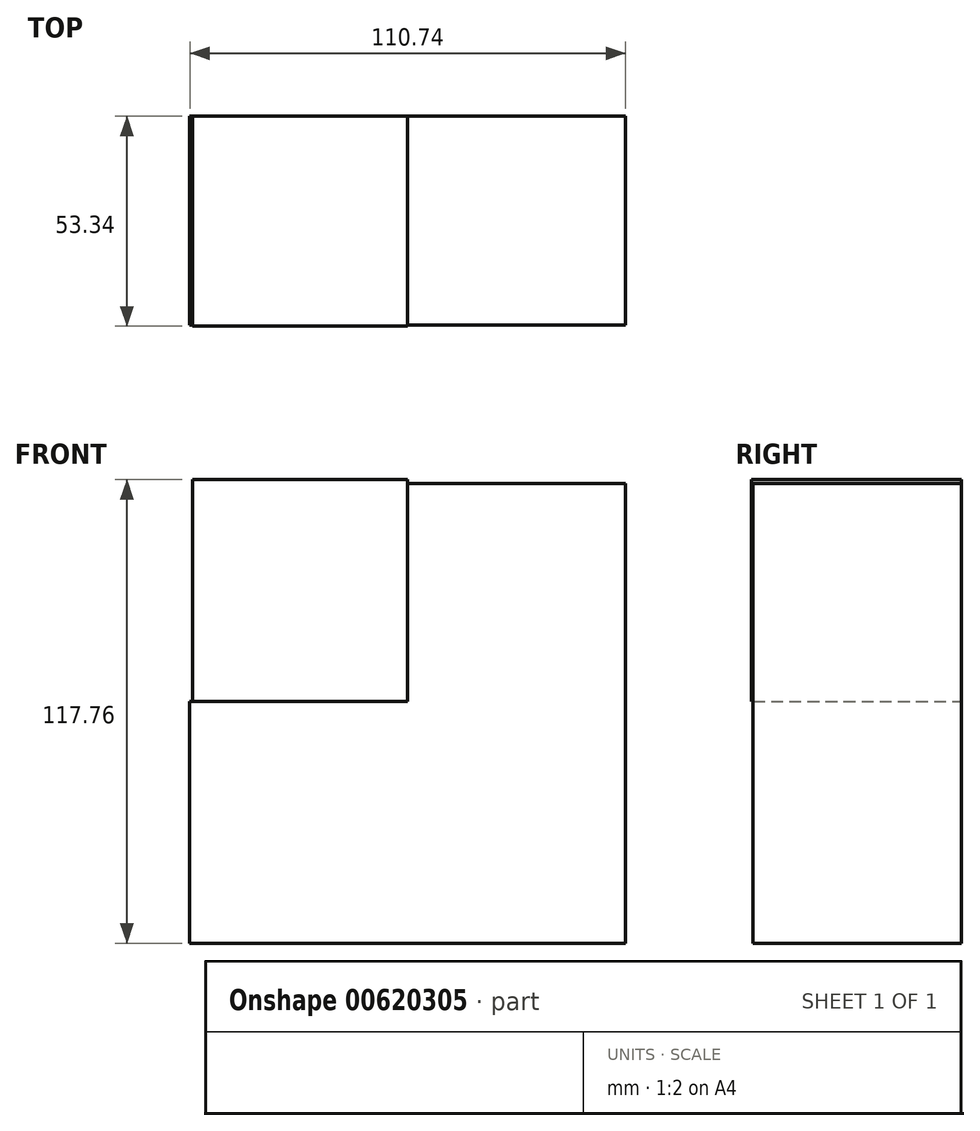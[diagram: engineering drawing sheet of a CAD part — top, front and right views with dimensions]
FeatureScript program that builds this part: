
annotation { "Feature Type Name" : "Feature", "Feature Type Description" : "" }
export const myFeature = defineFeature(function(context is Context, id is Id, definition is map)
    precondition{}
    {
        {
            var Q0;
            Q0=qCreatedBy(makeId("Right.planeOp"),FACE);
            var sketch = newSketch(context, id + "F0", { "sketchPlane" : qUnion([Q0])});
            skLineSegment(sketch, "E0.bottom", {"start": v(0, 0) * mm, "end": v(52.98, 0) * mm});
            skLineSegment(sketch, "E0.top", {"start": v(0, -61.46) * mm, "end": v(52.98, -61.46) * mm});
            skLineSegment(sketch, "E0.left", {"start": v(0, 0) * mm, "end": v(0, -61.46) * mm});
            skLineSegment(sketch, "E0.right", {"start": v(52.98, 0) * mm, "end": v(52.98, -61.46) * mm});
            skSolve(sketch);
        }
        {
            var Q0;
            Q0 = qSketchRegion(id + "F0", true);
            extrude(context, id + "F1", {"entities" : qUnion([Q0]), "oppositeDirection" : true, "depth" : 55.37 * mm, "offsetDistance" : 25.4 * mm});
        }
        {
            var Q0;
            Q0=makeQuery(id+"F1.opExtrude","SWEPT_FACE",FACE,{"disambiguationData":[OSD([sQuery(id+"F0.wireOp",EDGE,"E0.right")])]});
            var sketch = newSketch(context, id + "F2", { "sketchPlane" : qUnion([Q0])});
            skLineSegment(sketch, "E1.bottom", {"start": v(0, 0) * mm, "end": v(54.63, 0) * mm});
            skLineSegment(sketch, "E1.top", {"start": v(0, 56.3) * mm, "end": v(54.63, 56.3) * mm});
            skLineSegment(sketch, "E1.left", {"start": v(0, 0) * mm, "end": v(0, 56.3) * mm});
            skLineSegment(sketch, "E1.right", {"start": v(54.63, 0) * mm, "end": v(54.63, 56.3) * mm});
            skSolve(sketch);
        }
        {
            var Q0;
            Q0=makeQuery(id+"F2.imprint","IMPRINT",FACE,{"disambiguationData":[TD([[makeQuery(id+"F2.imprint","IMPRINT",EDGE,{"derivedFrom":sQuery(id+"F2.wireOp",EDGE,"E1.bottom")}),-1.0]])]});
            extrude(context, id + "F3", {"entities" : qUnion([Q0]), "operationType" : NewBodyOperationType.ADD, "oppositeDirection" : true, "depth" : 53.34 * mm, "offsetDistance" : 25.4 * mm});
        }
        {
            var Q0;
            Q0=makeQuery(id+"F3.boolean.opBoolean","MERGE",FACE,{"derivedFrom":[makeQuery(id+"F1.opExtrude","CAP_FACE",FACE,{"disambiguationData":[OSD([sQuery(id+"F0.wireOp",EDGE,"E0.bottom"),sQuery(id+"F0.wireOp",EDGE,"E0.top"),sQuery(id+"F0.wireOp",EDGE,"E0.left"),sQuery(id+"F0.wireOp",EDGE,"E0.right")])],"isStart":true}),makeQuery(id+"F3.opExtrude","SWEPT_FACE",FACE,{"disambiguationData":[OSD([sQuery(id+"F2.wireOp",EDGE,"E1.left")])]})]});
            var sketch = newSketch(context, id + "F4", { "sketchPlane" : qUnion([Q0])});
            skLineSegment(sketch, "E2.bottom", {"start": v(0, 0) * mm, "end": v(52.98, 0) * mm});
            skLineSegment(sketch, "E2.top", {"start": v(0, -61.46) * mm, "end": v(52.98, -61.46) * mm});
            skLineSegment(sketch, "E2.left", {"start": v(0, 0) * mm, "end": v(0, -61.46) * mm});
            skLineSegment(sketch, "E2.right", {"start": v(52.98, 0) * mm, "end": v(52.98, -61.46) * mm});
            skSolve(sketch);
        }
        {
            var Q0;
            Q0 = qSketchRegion(id + "F4", true);
            extrude(context, id + "F5", {"entities" : qUnion([Q0]), "operationType" : NewBodyOperationType.ADD, "depth" : 55.37 * mm, "offsetDistance" : 25.4 * mm});
        }
        {
            var Q0;
            Q0=makeQuery(id+"F5.opExtrude","SWEPT_FACE",FACE,{"disambiguationData":[OSD([sQuery(id+"F4.wireOp",EDGE,"E2.bottom")])]});
            var sketch = newSketch(context, id + "F6", { "sketchPlane" : qUnion([Q0])});
            skLineSegment(sketch, "E3.bottom", {"start": v(55.37, 0) * mm, "end": v(0, 0) * mm});
            skLineSegment(sketch, "E3.top", {"start": v(55.37, 52.98) * mm, "end": v(0, 52.98) * mm});
            skLineSegment(sketch, "E3.left", {"start": v(55.37, 0) * mm, "end": v(55.37, 52.98) * mm});
            skLineSegment(sketch, "E3.right", {"start": v(0, 0) * mm, "end": v(0, 52.98) * mm});
            skSolve(sketch);
        }
        {
            var Q0;
            Q0 = qSketchRegion(id + "F6", true);
            extrude(context, id + "F7", {"entities" : qUnion([Q0]), "operationType" : NewBodyOperationType.ADD, "depth" : 55.37 * mm, "offsetDistance" : 25.4 * mm});
        }
    });
